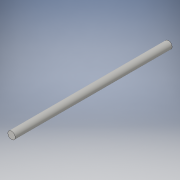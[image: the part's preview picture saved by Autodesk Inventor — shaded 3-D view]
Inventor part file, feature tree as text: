
AUTODESK INVENTOR PART (.ipt)
format: ipt  version: 2016 (Build 200138000, 138)  size: 86,528 bytes
history: native  units: in
note: dims shown in document units (in); Inventor stores cm internally (conversion verified against a paired STEP export)
features: extrude x1, sketch x1
ambient origin geometry x8: Origin, YZ Plane, XZ Plane, XY Plane, X Axis, Y Axis, Z Axis, Center Point
bodies: Solid1 (feature_tree)
feature tree (2):
  extrude  "Extrusion1"  Depth=4.0in TaperAngle=0.0deg
  sketch  "Sketch1"  dims[d0=0.188in d1=4.0in d2=0.0in]
